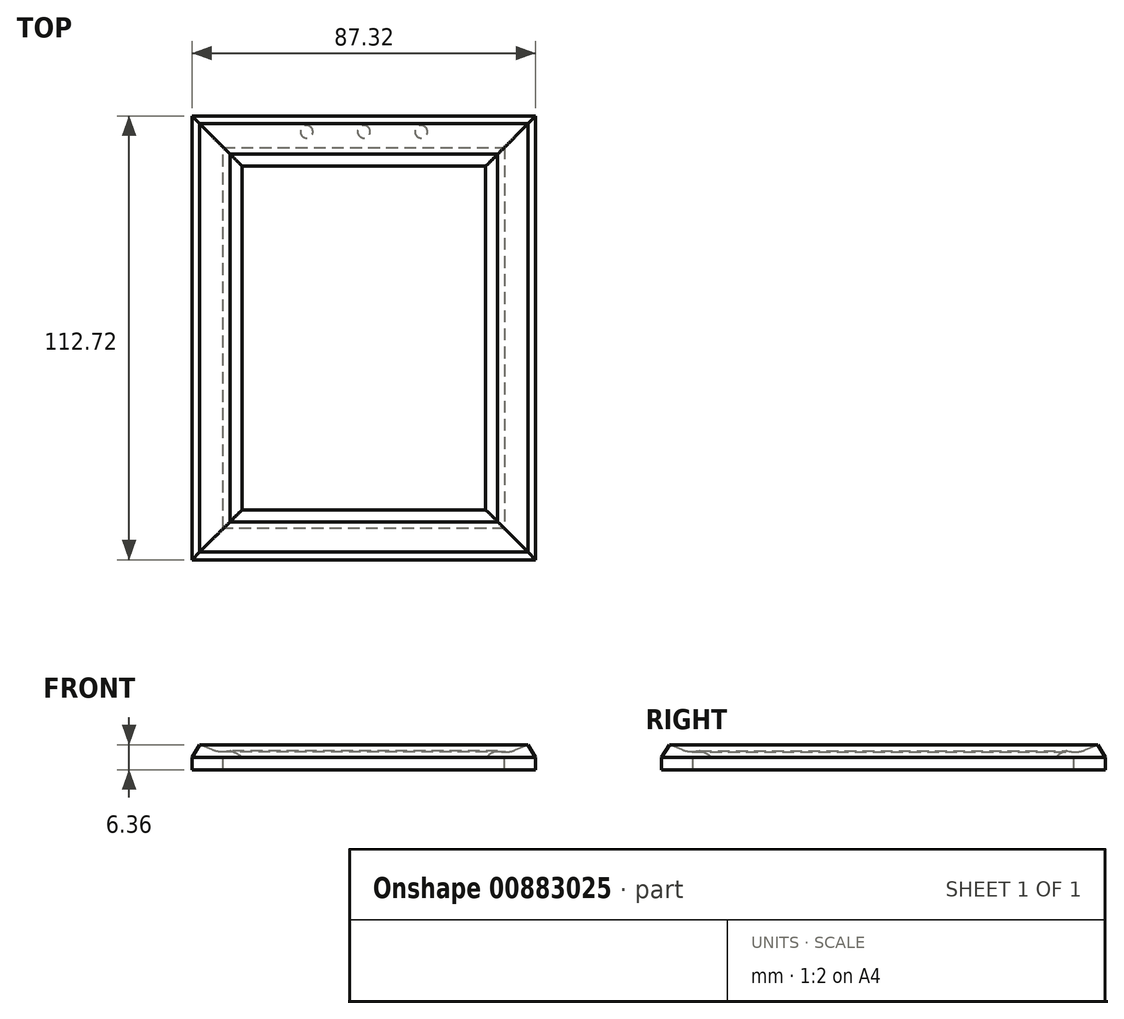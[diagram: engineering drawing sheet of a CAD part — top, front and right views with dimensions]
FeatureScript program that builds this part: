
annotation { "Feature Type Name" : "Feature", "Feature Type Description" : "" }
export const myFeature = defineFeature(function(context is Context, id is Id, definition is map)
    precondition{}
    {
        {
            var Q0;
            Q0=qCreatedBy(makeId("Top.planeOp"),FACE);
            var sketch = newSketch(context, id + "F0", { "sketchPlane" : qUnion([Q0])});
            skLineSegment(sketch, "E0.bottom", {"start": v(35.72, -48.42) * mm, "end": v(-35.72, -48.42) * mm});
            skLineSegment(sketch, "E0.top", {"start": v(35.72, 48.42) * mm, "end": v(-35.72, 48.42) * mm});
            skLineSegment(sketch, "E0.left", {"start": v(35.72, -48.42) * mm, "end": v(35.72, 48.42) * mm});
            skLineSegment(sketch, "E0.right", {"start": v(-35.72, -48.42) * mm, "end": v(-35.72, 48.42) * mm});
            skPoint(sketch, "E0.middle", {"position": v(0, 0) * mm});
            skLineSegment(sketch, "E1.bottom", {"start": v(30.96, 43.66) * mm, "end": v(-30.96, 43.66) * mm});
            skLineSegment(sketch, "E1.top", {"start": v(30.96, -43.66) * mm, "end": v(-30.96, -43.66) * mm});
            skLineSegment(sketch, "E1.left", {"start": v(30.96, 43.66) * mm, "end": v(30.96, -43.66) * mm});
            skLineSegment(sketch, "E1.right", {"start": v(-30.96, 43.66) * mm, "end": v(-30.96, -43.66) * mm});
            skLineSegment(sketch, "E2.0", {"start": v(43.66, 56.36) * mm, "end": v(-43.66, 56.36) * mm});
            skLineSegment(sketch, "E2.1", {"start": v(43.66, 56.36) * mm, "end": v(43.66, -56.36) * mm});
            skLineSegment(sketch, "E2.2", {"start": v(43.66, -56.36) * mm, "end": v(-43.66, -56.36) * mm});
            skLineSegment(sketch, "E2.3", {"start": v(-43.66, 56.36) * mm, "end": v(-43.66, -56.36) * mm});
            skSolve(sketch);
        }
        {
            var Q0;
            Q0=qCreatedBy(makeId("Front.planeOp"),FACE);
            var sketch = newSketch(context, id + "F1", { "sketchPlane" : qUnion([Q0])});
            skPoint(sketch, "E3.0", {"position": v(43.66, 0) * mm});
            skPoint(sketch, "E4.0", {"position": v(30.96, 0) * mm});
            skLineSegment(sketch, "E5", {"start": v(30.96, 0) * mm, "end": v(43.66, 0) * mm, "construction": true});
            skLineSegment(sketch, "E6.bottom", {"start": v(43.66, 3.18) * mm, "end": v(30.96, 3.17) * mm, "construction": true});
            skLineSegment(sketch, "E6.top", {"start": v(43.66, -3.17) * mm, "end": v(30.96, -3.18) * mm, "construction": true});
            skLineSegment(sketch, "E6.left", {"start": v(43.66, 3.18) * mm, "end": v(43.66, -3.17) * mm, "construction": true});
            skLineSegment(sketch, "E6.right", {"start": v(30.96, 3.17) * mm, "end": v(30.96, -3.18) * mm, "construction": true});
            skLineSegment(sketch, "E7.bottom", {"start": v(30.96, 0) * mm, "end": v(35.72, 0) * mm});
            skLineSegment(sketch, "E7.top", {"start": v(30.96, -3.17) * mm, "end": v(35.72, -3.17) * mm, "construction": true});
            skLineSegment(sketch, "E7.left", {"start": v(30.96, 0) * mm, "end": v(30.96, -3.18) * mm, "construction": true});
            skLineSegment(sketch, "E7.right", {"start": v(35.72, 0) * mm, "end": v(35.72, -3.17) * mm});
            skPoint(sketch, "E8.0", {"position": v(35.72, 0) * mm});
            skLineSegment(sketch, "E9", {"start": v(35.72, -3.17) * mm, "end": v(43.66, -3.17) * mm});
            skLineSegment(sketch, "E10", {"start": v(43.66, -3.17) * mm, "end": v(43.66, 0) * mm});
            skLineSegment(sketch, "E11", {"start": v(43.66, 0) * mm, "end": v(41.71, 3.17) * mm});
            skLineSegment(sketch, "E12", {"start": v(41.71, 3.17) * mm, "end": v(38.42, 1.82) * mm});
            skLineSegment(sketch, "E13", {"start": v(34.42, 1.54) * mm, "end": v(34, 1.65) * mm});
            skLineSegment(sketch, "E14", {"start": v(34, 1.65) * mm, "end": v(33.9, 1.62) * mm});
            skLineSegment(sketch, "E15", {"start": v(31.6, 0.5) * mm, "end": v(30.96, 0) * mm});
            skPoint(sketch, "E16.visualSharp", {"position": v(32.64, 1.3) * mm});
            skArc(sketch, "E16.filletArc", {"start": v(33.9, 1.62) * mm, "mid": v(32.7, 1.18) * mm, "end": v(31.6, 0.5) * mm});
            skPoint(sketch, "E17.visualSharp", {"position": v(36.47, 1.01) * mm});
            skArc(sketch, "E17.filletArc", {"start": v(34.42, 1.54) * mm, "mid": v(36.44, 1.35) * mm, "end": v(38.42, 1.82) * mm});
            skSolve(sketch);
        }
        {
            var Q0;
            Q0=makeQuery(id+"F1.imprint","IMPRINT",FACE,{"disambiguationData":[TD([[makeQuery(id+"F1.imprint","IMPRINT",EDGE,{"derivedFrom":sQuery(id+"F1.wireOp",EDGE,"E7.bottom")}),1.0]])]});
            var Q1;
            Q1=sQuery(id+"F0.wireOp",EDGE,"E0.left");
            var Q2;
            Q2=sQuery(id+"F0.wireOp",EDGE,"E0.top");
            var Q3;
            Q3=sQuery(id+"F0.wireOp",EDGE,"E0.right");
            var Q4;
            Q4=sQuery(id+"F0.wireOp",EDGE,"E0.bottom");
            sweep(context, id + "F2", {"profiles" : qUnion([Q0]), "path" : qUnion([Q1, Q2, Q3, Q4])});
        }
        {
            assignVariable(context, id + "F3", {"name" : "batteryThickness", "anyValue" : 1 / 406.4 * mm});
        }
        {
            var Q0;
            Q0=makeQuery(id+"F2.opSweep","SWEPT_FACE",FACE,{"disambiguationData":[OSD([sQuery(id+"F0.wireOp",EDGE,"E0.bottom"),sQuery(id+"F1.wireOp",EDGE,"E9")])]});
            var sketch = newSketch(context, id + "F4", { "sketchPlane" : qUnion([Q0])});
            skLineSegment(sketch, "E18.0.0", {"start": v(-43.66, -56.36) * mm, "end": v(43.66, -56.36) * mm});
            skLineSegment(sketch, "E18.0.1", {"start": v(43.66, -56.36) * mm, "end": v(43.66, 56.36) * mm});
            skLineSegment(sketch, "E18.0.2", {"start": v(43.66, 56.36) * mm, "end": v(-43.66, 56.36) * mm});
            skLineSegment(sketch, "E18.0.3", {"start": v(-43.66, 56.36) * mm, "end": v(-43.66, -56.36) * mm});
            skLineSegment(sketch, "E19.0.0", {"start": v(35.72, 48.42) * mm, "end": v(35.72, -48.42) * mm});
            skLineSegment(sketch, "E19.0.1", {"start": v(35.72, -48.42) * mm, "end": v(-35.72, -48.42) * mm});
            skLineSegment(sketch, "E19.0.2", {"start": v(-35.72, -48.42) * mm, "end": v(-35.72, 48.42) * mm});
            skLineSegment(sketch, "E19.0.3", {"start": v(-35.72, 48.42) * mm, "end": v(35.72, 48.42) * mm});
            skLineSegment(sketch, "E20", {"start": v(0, 56.36) * mm, "end": v(0, 48.42) * mm, "construction": true});
            skCircle(sketch, "E21", {"center": v(0, 52.39) * mm, "radius": 1.59 * mm});
            skLineSegment(sketch, "E22", {"start": v(-14.55, 52.39) * mm, "end": v(14.55, 52.39) * mm, "construction": true});
            skCircle(sketch, "E23", {"center": v(-14.55, 52.39) * mm, "radius": 1.59 * mm});
            skCircle(sketch, "E24", {"center": v(14.55, 52.39) * mm, "radius": 1.59 * mm});
            skLineSegment(sketch, "E25", {"start": v(-43.66, 0) * mm, "end": v(43.66, 0) * mm, "construction": true});
            skCircle(sketch, "E26.MirrorC", {"center": v(-14.55, -52.39) * mm, "radius": 1.59 * mm});
            skCircle(sketch, "E27.MirrorC", {"center": v(0, -52.39) * mm, "radius": 1.59 * mm});
            skCircle(sketch, "E28.MirrorC", {"center": v(14.55, -52.39) * mm, "radius": 1.59 * mm});
            skSolve(sketch);
        }
        {
            var Q0;
            Q0=makeQuery(id+"F4.imprint","IMPRINT",FACE,{"disambiguationData":[TD([[makeQuery(id+"F4.imprint","IMPRINT",EDGE,{"derivedFrom":sQuery(id+"F4.wireOp",EDGE,"E23")}),1.0]])]});
            var Q1;
            Q1=makeQuery(id+"F4.imprint","IMPRINT",FACE,{"disambiguationData":[TD([[makeQuery(id+"F4.imprint","IMPRINT",EDGE,{"derivedFrom":sQuery(id+"F4.wireOp",EDGE,"E21")}),1.0]])]});
            var Q2;
            Q2=makeQuery(id+"F4.imprint","IMPRINT",FACE,{"disambiguationData":[TD([[makeQuery(id+"F4.imprint","IMPRINT",EDGE,{"derivedFrom":sQuery(id+"F4.wireOp",EDGE,"E24")}),1.0]])]});
            var Q3;
            Q3=makeQuery(id+"F4.imprint","IMPRINT",FACE,{"disambiguationData":[TD([[makeQuery(id+"F4.imprint","IMPRINT",EDGE,{"derivedFrom":sQuery(id+"F4.wireOp",EDGE,"E26.MirrorC")}),-1.0]])]});
            var Q4;
            Q4=makeQuery(id+"F4.imprint","IMPRINT",FACE,{"disambiguationData":[TD([[makeQuery(id+"F4.imprint","IMPRINT",EDGE,{"derivedFrom":sQuery(id+"F4.wireOp",EDGE,"E27.MirrorC")}),-1.0]])]});
            var Q5;
            Q5=makeQuery(id+"F4.imprint","IMPRINT",FACE,{"disambiguationData":[TD([[makeQuery(id+"F4.imprint","IMPRINT",EDGE,{"derivedFrom":sQuery(id+"F4.wireOp",EDGE,"E28.MirrorC")}),-1.0]])]});
            extrude(context, id + "F5", {"entities" : qUnion([Q0, Q1, Q2, Q3, Q4, Q5]), "operationType" : NewBodyOperationType.REMOVE, "oppositeDirection" : true, "depth" : getVariable(context, 'batteryThickness') / 2, "offsetDistance" : 25.4 * mm});
        }
    });
